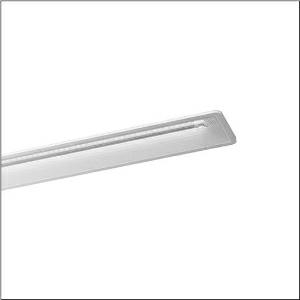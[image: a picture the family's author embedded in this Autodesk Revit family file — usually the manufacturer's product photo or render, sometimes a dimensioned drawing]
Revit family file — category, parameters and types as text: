
# Revit family: taris_r__21_5mt117d03wd_677e
name_source: partatom
category: Lighting Fixtures
units: mm (PartAtom-declared; Revit-internal decimal feet)

## family parameters
Cut with Voids When Loaded = No
Host = Face
Light Source = No
Part Type = Normal
Room Calculation Point = No
Round Connector Dimension = Use Diameter
Shared = No

## types (1)
- --- (1 x LED, 5700 lm, 35.9 W, 3000K)
    Apparent Load = 36 VA
    CIE Flux Codes = 73 96 99 100 100
    Color Rendering = 80
    Color Temperature = 3000K
    Default Elevation = 1800 mm
    Description = Taris® 21, office luminaire, primary anti-glare with micro louvre, primary optical cover: axial lens, of PMMA, structured, CAT 2 (L<= 1500cd/m²), light emission: direct distribution, primary light characteristic: symmetric, installation type: recessed, LED rated luminous flux: 5.700 lm, light colour: 830, colour temperature: 3000K, control gear: ECG DALI, with terminal, 5-pole, mains connection: 230V, AC, 50Hz, rated input power: 36W, housing, luminaire housing, of plastic, pure white, length: 1.530 mm, width: 150 mm, height: 76mm, recess depth: 106 mm, protection rating (complete): IP20, insulation class (complete): insulation class I (protective earthing), certification: CE, ENEC, VDE, protection symbol: F, impact resistance: IK02, permissible ambient temperature for indoor applications: 0..+35°C, standard: EN 50419, packaging unit: 1 piece
    Height = 0 mm  [stored 0 ft]
    Lamp = 1 x LED
    Lamp Light Flux = 5700 lm
    Lamp Power = 35.9 W
    Lamp count = 1
    Length = 1524 mm  [stored 5 ft]
    Luminous efficacy = 159 lm/W
    Manufacturer = Siteco
    ModVariant = No
    Model = 5MT117D03WD
    Mounting Place = Ceiling
    Mounting Type = Recessed
    Number of Poles = 1
    OnlyDefault = Yes
    Power Factor = 1
    Product Name = Taris® 21
    Product group = office luminaire | ceiling recessed
    ProductGroupID = 400
    Protection Class = Protection class I
    Protection Degree = IP 20
    RLX_Detail_Level = 1
    RlxData = <blob elided: 30377 chars, md5=cbe288fe>
    Socket = socket
    Standby Power = 0 W
    System Light Flux = 5700 lm
    System Power = 36 W
    Type Comments = factory setting: luminous flux: 100 % | dim-lin: 254 | 200 mA
    Type Image = l_1004723.jpg
    URL = http://relux.com
    VarID = @adj_130149
    Voltage = 0 V
    Weight = 0.00 kg
    Width = 144 mm

note: [stored X ft] marks values corroborated as IEEE doubles in the binary element streams (Revit-internal decimal feet)

## geometry (parser evidence)
native form markers: Blend x4, Sweep x8
no freeform markers — native parametric forms only
